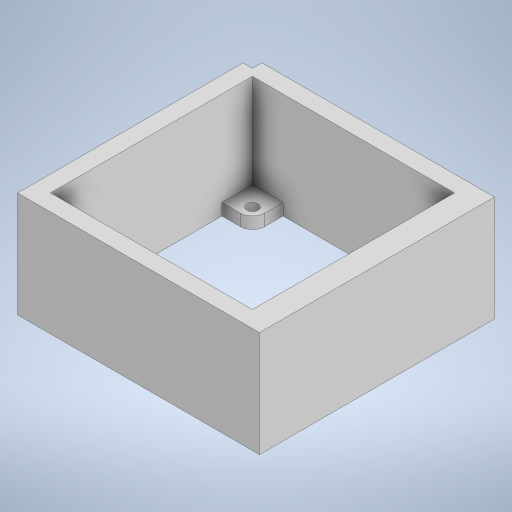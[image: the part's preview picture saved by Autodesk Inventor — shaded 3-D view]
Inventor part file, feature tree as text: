
AUTODESK INVENTOR PART (.ipt)
format: ipt  version: 2024 (Build 280153000, 153)  size: 307,200 bytes
history: native  units: mm
features: extrude x6, sketch x6, projected_geometry x6, shell x1, fillet x1
ambient origin geometry x8: Origin, YZ Plane, XZ Plane, XY Plane, X Axis, Y Axis, Z Axis, Center Point
bodies: Solid1 (feature_tree)
feature tree (20):
  extrude  "Extrusion1"  Depth=86.0mm
  shell  "Shell1"  Thickness=92.0mm
  extrude  "Extrusion2"  Depth=3.0mm
  extrude  "Extrusion3"  Depth=13.0mm
  fillet  "Fillet1"  Radius=13.0mm
  extrude  "Extrusion4"  Depth=40.0mm TaperAngle=0.0deg
  extrude  "Extrusion5"  Depth=4.8mm
  extrude  "Extrusion6"  Depth=4.0mm
  sketch  "Sketch1"  dims[d0=86.0mm d1=86.0mm d2=92.0mm]
  sketch  "Sketch3"  dims[d3=45.0mm d4=0.0mm d5=3.0mm]
  sketch  "Sketch4"  dims[d6=13.0mm d7=13.0mm d8=13.0mm]
  projected_geometry  "Projected Loop1"
  sketch  "Sketch5"  dims[d9=13.0mm d10=40.0mm d11=0.0mm]
  projected_geometry  "Projected Loop2"
  sketch  "Sketch6"  dims[d12=69.6mm d13=4.8mm]
  sketch  "Sketch7"  dims[d14=4.8mm d15=4.8mm d16=4.8mm d17=25.0mm d18=0.0mm d19=5.0mm d20=7.0mm d21=0.0mm d22=4.0mm d23=4.0mm d24=10.0mm d25=0.0mm d26=4.0mm d27=2.0mm d28=0.0mm]
  projected_geometry  "Projected Loop3"
  projected_geometry  "Projected Loop4"
  projected_geometry  "Projected Loop5"
  projected_geometry  "Projected Loop6"
